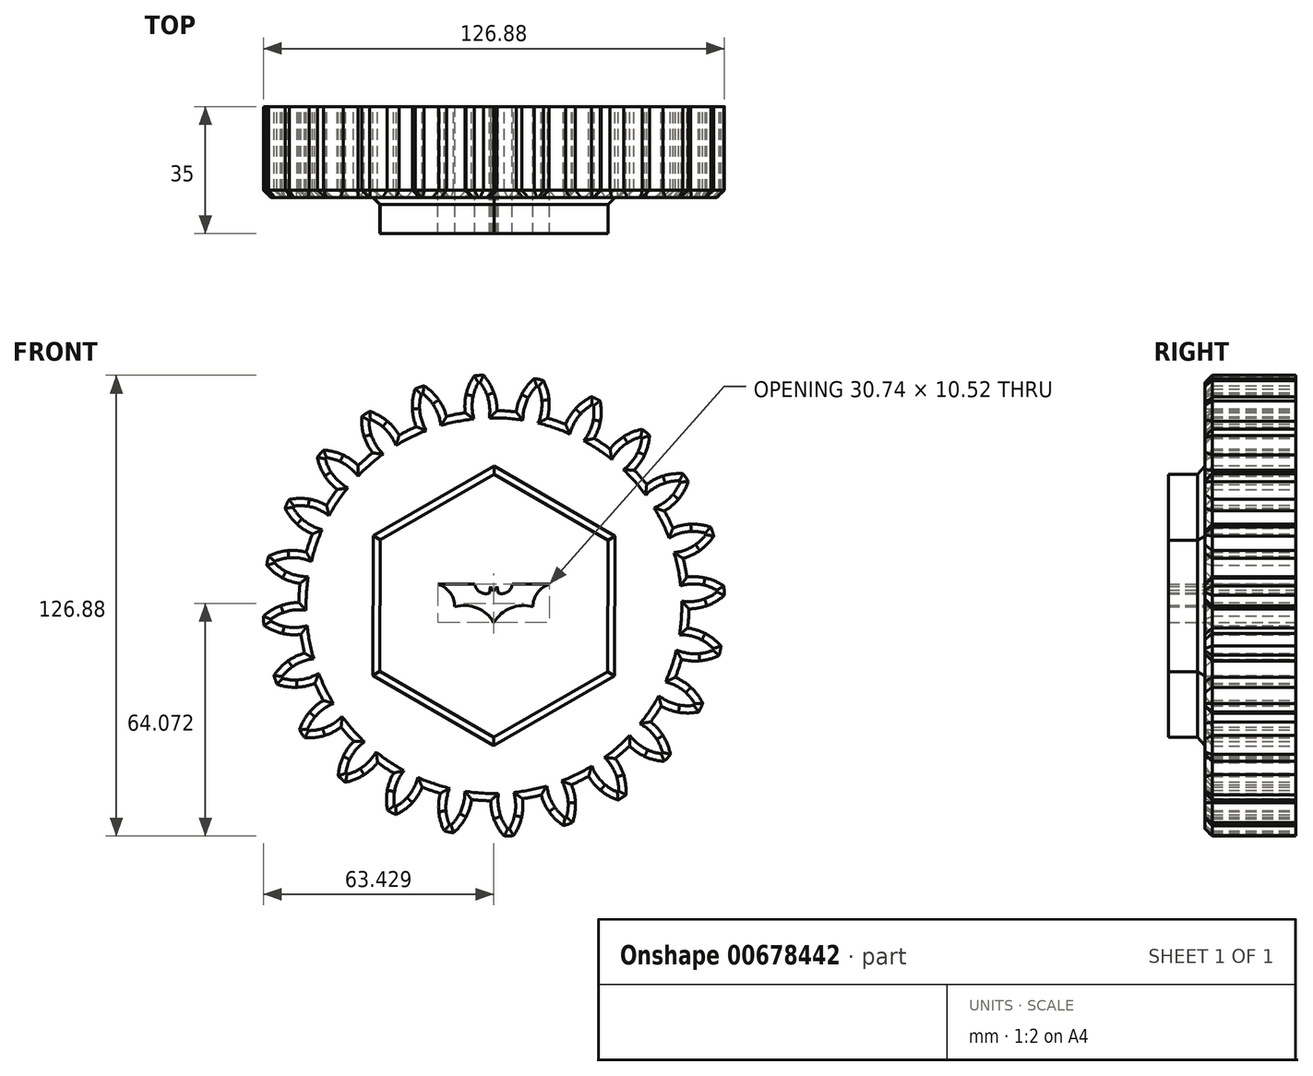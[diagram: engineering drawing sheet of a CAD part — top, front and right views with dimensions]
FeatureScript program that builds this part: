
annotation { "Feature Type Name" : "Feature", "Feature Type Description" : "" }
export const myFeature = defineFeature(function(context is Context, id is Id, definition is map)
    precondition{}
    {
        {
            var Q0;
            Q0=qCreatedBy(makeId("Front.planeOp"),FACE);
            var sketch = newSketch(context, id + "F0", { "sketchPlane" : qUnion([Q0])});
            skCircle(sketch, "E0", {"center": v(0, 0) * mm, "radius": 53.72 * mm});
            skCircle(sketch, "E1", {"center": v(0, 0) * mm, "radius": 58.67 * mm, "construction": true});
            skCircle(sketch, "E2", {"center": v(0, 0) * mm, "radius": 63.5 * mm, "construction": true});
            skLineSegment(sketch, "E3", {"start": v(0, 0) * mm, "end": v(0, 90.99) * mm, "construction": true});
            skLineSegment(sketch, "E4", {"start": v(0, 0) * mm, "end": v(-6.34, 96.72) * mm, "construction": true});
            skLineSegment(sketch, "E5", {"start": v(0, 58.67) * mm, "end": v(-59.75, 58.67) * mm, "construction": true});
            skLineSegment(sketch, "E6", {"start": v(0, 58.67) * mm, "end": v(-56.6, 38.07) * mm, "construction": true});
            skCircle(sketch, "E7", {"center": v(0, 0) * mm, "radius": 55.14 * mm, "construction": true});
            skCircle(sketch, "E8", {"center": v(0, 58.67) * mm, "radius": 14.6 * mm, "construction": true});
            skCircle(sketch, "E9", {"center": v(-13.72, 53.68) * mm, "radius": 14.6 * mm, "construction": true});
            skArc(sketch, "E10", {"start": v(0, 58.67) * mm, "mid": v(-1.2, 61.19) * mm, "end": v(-2.86, 63.44) * mm});
            skArc(sketch, "E11", {"start": v(0.88, 53.71) * mm, "mid": v(0.65, 56.23) * mm, "end": v(0, 58.67) * mm});
            skArc(sketch, "E12.MirrorCS", {"start": v(-7.66, 58.17) * mm, "mid": v(-6.8, 60.82) * mm, "end": v(-5.45, 63.27) * mm});
            skArc(sketch, "E13.MirrorCS", {"start": v(-7.88, 53.14) * mm, "mid": v(-7.98, 55.67) * mm, "end": v(-7.66, 58.17) * mm});
            skArc(sketch, "E14", {"start": v(-2.86, 63.44) * mm, "mid": v(-4.16, 63.41) * mm, "end": v(-5.45, 63.27) * mm});
            skCircle(sketch, "E15.cCircle", {"center": v(0, 0) * mm, "radius": 31.32 * mm, "construction": true});
            skLineSegment(sketch, "E15.0", {"start": v(31.27, -18.18) * mm, "end": v(-0.1, -36.17) * mm});
            skLineSegment(sketch, "E15.1", {"start": v(-0.1, -36.17) * mm, "end": v(-31.37, -18) * mm});
            skLineSegment(sketch, "E15.2", {"start": v(-31.37, -18) * mm, "end": v(-31.27, 18.18) * mm});
            skLineSegment(sketch, "E15.3", {"start": v(-31.27, 18.18) * mm, "end": v(0.1, 36.17) * mm});
            skLineSegment(sketch, "E15.4", {"start": v(0.1, 36.17) * mm, "end": v(31.37, 18) * mm});
            skLineSegment(sketch, "E15.5", {"start": v(31.37, 18) * mm, "end": v(31.27, -18.18) * mm});
            skPoint(sketch, "E15.0.midPoint", {"position": v(15.58, -27.17) * mm});
            skLineSegment(sketch, "E16", {"start": v(-15.38, 5.9) * mm, "end": v(-5.26, 5.9) * mm});
            skLineSegment(sketch, "E17", {"start": v(5.05, 5.9) * mm, "end": v(15.36, 5.9) * mm});
            skLineSegment(sketch, "E18", {"start": v(-0.9, 5.3) * mm, "end": v(-1.23, 3.48) * mm});
            skLineSegment(sketch, "E19", {"start": v(0.82, 5.3) * mm, "end": v(1.22, 3.48) * mm});
            skLineSegment(sketch, "E20", {"start": v(-0.9, 5.3) * mm, "end": v(-0.56, 4.35) * mm});
            skLineSegment(sketch, "E21", {"start": v(-0.56, 4.35) * mm, "end": v(0.45, 4.35) * mm});
            skLineSegment(sketch, "E22", {"start": v(0.45, 4.35) * mm, "end": v(0.82, 5.3) * mm});
            skArc(sketch, "E23", {"start": v(-5.26, 5.9) * mm, "mid": v(-3.8, 3.76) * mm, "end": v(-1.23, 3.48) * mm});
            skArc(sketch, "E24", {"start": v(1.22, 3.48) * mm, "mid": v(3.72, 3.76) * mm, "end": v(5.05, 5.9) * mm});
            skPoint(sketch, "E25", {"position": v(-10.78, -0.27) * mm});
            skPoint(sketch, "E26", {"position": v(10.74, -0.27) * mm});
            skPoint(sketch, "E27", {"position": v(0, -4.63) * mm});
            skArc(sketch, "E28", {"start": v(-10.78, -0.27) * mm, "mid": v(-12.05, 3.58) * mm, "end": v(-15.38, 5.9) * mm});
            skArc(sketch, "E29", {"start": v(15.36, 5.9) * mm, "mid": v(12, 3.6) * mm, "end": v(10.74, -0.27) * mm});
            skArc(sketch, "E30", {"start": v(0, -4.63) * mm, "mid": v(-4.66, -0.63) * mm, "end": v(-10.78, -0.27) * mm});
            skArc(sketch, "E31", {"start": v(10.74, -0.27) * mm, "mid": v(4.64, -0.65) * mm, "end": v(0, -4.63) * mm});
            skSolve(sketch);
        }
        {
            var Q0;
            Q0=makeQuery(id+"F0.imprint","IMPRINT",FACE,{"disambiguationData":[TD([[makeQuery(id+"F0.imprint","IMPRINT",EDGE,{"derivedFrom":sQuery(id+"F0.wireOp",EDGE,"E10")}),1.0]])]});
            var Q1;
            {var subQ0=sQuery(id+"F0.wireOp",EDGE,"E0");var subQ1=makeQuery(id+"F0.imprint","INTERSECT",VERTEX,{"derivedFrom":[subQ0,sQuery(id+"F0.wireOp",EDGE,"E11")]});Q1=makeQuery(id+"F0.imprint","IMPRINT",FACE,{"disambiguationData":[TD([[makeQuery(id+"F0.imprint","IMPRINT",EDGE,{"disambiguationData":[TD([[subQ1,-1.0]])],"derivedFrom":subQ0}),1.0]])]});}
            extrude(context, id + "F1", {"entities" : qUnion([Q0, Q1]), "depth" : 25 * mm, "offsetDistance" : 25 * mm});
        }
        {
            var Q0;
            Q0=makeQuery(id+"F1.opExtrude","SWEPT_BODY",BODY,{"disambiguationData":[OSD([sQuery(id+"F0.wireOp",EDGE,"E0"),sQuery(id+"F0.wireOp",EDGE,"E10"),sQuery(id+"F0.wireOp",EDGE,"E11"),sQuery(id+"F0.wireOp",EDGE,"E12.MirrorCS"),sQuery(id+"F0.wireOp",EDGE,"E13.MirrorCS"),sQuery(id+"F0.wireOp",EDGE,"E14")])]});
            var Q1;
            Q1=makeQuery(id+"F1.opExtrude","SWEPT_FACE",FACE,{"disambiguationData":[OSD([sQuery(id+"F0.wireOp",EDGE,"E0")])]});
            circularPattern(context, id + "F2", {"entities" : qUnion([Q0]), "axis" : qUnion([Q1]), "angle" : 360 * degree, "instanceCount" : 24, "equalSpace" : true});
        }
        {
            var Q0;
            Q0=makeQuery(id+"F0.imprint","IMPRINT",FACE,{"disambiguationData":[TD([[makeQuery(id+"F0.imprint","IMPRINT",EDGE,{"derivedFrom":sQuery(id+"F0.wireOp",EDGE,"E15.0")}),-1.0]])]});
            extrude(context, id + "F3", {"entities" : qUnion([Q0]), "operationType" : NewBodyOperationType.ADD, "depth" : 35 * mm, "offsetDistance" : 25 * mm});
        }
        {
            var Q0;
            {var subQ0=makeQuery(id+"F1.opExtrude","CAP_FACE",FACE,{"disambiguationData":[OSD([sQuery(id+"F0.wireOp",EDGE,"E0"),sQuery(id+"F0.wireOp",EDGE,"E10"),sQuery(id+"F0.wireOp",EDGE,"E11"),sQuery(id+"F0.wireOp",EDGE,"E12.MirrorCS"),sQuery(id+"F0.wireOp",EDGE,"E13.MirrorCS"),sQuery(id+"F0.wireOp",EDGE,"E14"),sQuery(id+"F0.wireOp",EDGE,"E15.0"),sQuery(id+"F0.wireOp",EDGE,"E15.1"),sQuery(id+"F0.wireOp",EDGE,"E15.2"),sQuery(id+"F0.wireOp",EDGE,"E15.3"),sQuery(id+"F0.wireOp",EDGE,"E15.4"),sQuery(id+"F0.wireOp",EDGE,"E15.5")])],"isStart":false});Q0=makeQuery(id+"F3.boolean.opBoolean","MERGE",FACE,{"derivedFrom":[subQ0,makeQuery(id+"F2.opPattern","COPY",FACE,{"derivedFrom":subQ0,"instanceName":"1"}),makeQuery(id+"F2.opPattern","COPY",FACE,{"derivedFrom":subQ0,"instanceName":"2"}),makeQuery(id+"F2.opPattern","COPY",FACE,{"derivedFrom":subQ0,"instanceName":"3"}),makeQuery(id+"F2.opPattern","COPY",FACE,{"derivedFrom":subQ0,"instanceName":"4"}),makeQuery(id+"F2.opPattern","COPY",FACE,{"derivedFrom":subQ0,"instanceName":"5"}),makeQuery(id+"F2.opPattern","COPY",FACE,{"derivedFrom":subQ0,"instanceName":"6"}),makeQuery(id+"F2.opPattern","COPY",FACE,{"derivedFrom":subQ0,"instanceName":"7"}),makeQuery(id+"F2.opPattern","COPY",FACE,{"derivedFrom":subQ0,"instanceName":"8"}),makeQuery(id+"F2.opPattern","COPY",FACE,{"derivedFrom":subQ0,"instanceName":"9"}),makeQuery(id+"F2.opPattern","COPY",FACE,{"derivedFrom":subQ0,"instanceName":"10"}),makeQuery(id+"F2.opPattern","COPY",FACE,{"derivedFrom":subQ0,"instanceName":"11"}),makeQuery(id+"F2.opPattern","COPY",FACE,{"derivedFrom":subQ0,"instanceName":"12"}),makeQuery(id+"F2.opPattern","COPY",FACE,{"derivedFrom":subQ0,"instanceName":"13"}),makeQuery(id+"F2.opPattern","COPY",FACE,{"derivedFrom":subQ0,"instanceName":"14"}),makeQuery(id+"F2.opPattern","COPY",FACE,{"derivedFrom":subQ0,"instanceName":"15"}),makeQuery(id+"F2.opPattern","COPY",FACE,{"derivedFrom":subQ0,"instanceName":"16"}),makeQuery(id+"F2.opPattern","COPY",FACE,{"derivedFrom":subQ0,"instanceName":"17"}),makeQuery(id+"F2.opPattern","COPY",FACE,{"derivedFrom":subQ0,"instanceName":"18"}),makeQuery(id+"F2.opPattern","COPY",FACE,{"derivedFrom":subQ0,"instanceName":"19"}),makeQuery(id+"F2.opPattern","COPY",FACE,{"derivedFrom":subQ0,"instanceName":"20"}),makeQuery(id+"F2.opPattern","COPY",FACE,{"derivedFrom":subQ0,"instanceName":"21"}),makeQuery(id+"F2.opPattern","COPY",FACE,{"derivedFrom":subQ0,"instanceName":"22"}),makeQuery(id+"F2.opPattern","COPY",FACE,{"derivedFrom":subQ0,"instanceName":"23"})]});}
            chamfer(context, id + "F4", {"entities" : qUnion([Q0]), "width" : 2 * mm, "tangentPropagation" : true});
        }
    });
